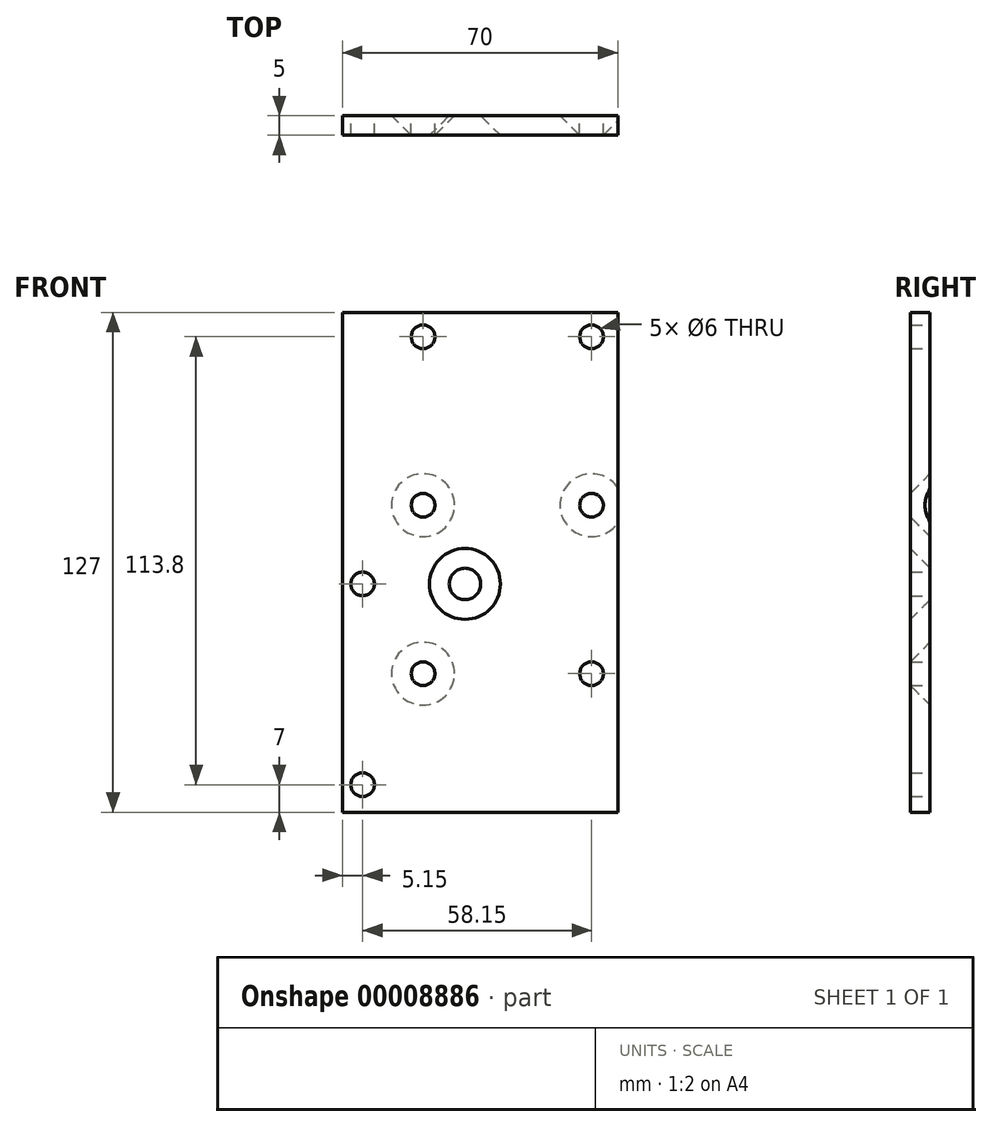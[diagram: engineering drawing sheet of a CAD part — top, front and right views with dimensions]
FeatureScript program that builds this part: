
annotation { "Feature Type Name" : "Feature", "Feature Type Description" : "" }
export const myFeature = defineFeature(function(context is Context, id is Id, definition is map)
    precondition{}
    {
        {
            var Q0;
            Q0=qCreatedBy(makeId("Front.planeOp"),FACE);
            var sketch = newSketch(context, id + "F0", { "sketchPlane" : qUnion([Q0])});
            skLineSegment(sketch, "E0.bottom", {"start": v(-35, 63.5) * mm, "end": v(35, 63.5) * mm});
            skLineSegment(sketch, "E0.top", {"start": v(-35, -63.5) * mm, "end": v(35, -63.5) * mm});
            skLineSegment(sketch, "E0.left", {"start": v(-35, 63.5) * mm, "end": v(-35, -63.5) * mm});
            skLineSegment(sketch, "E0.right", {"start": v(35, 63.5) * mm, "end": v(35, -63.5) * mm});
            skPoint(sketch, "E0.middle", {"position": v(0, 0) * mm});
            skCircle(sketch, "E1", {"center": v(28.3, -28.3) * mm, "radius": 3 * mm});
            skCircle(sketch, "E2.1.0", {"center": v(28.3, 14.5) * mm, "radius": 3 * mm});
            skCircle(sketch, "E2.2.0", {"center": v(-14.5, 14.5) * mm, "radius": 3 * mm});
            skCircle(sketch, "E2.3.0", {"center": v(-14.5, -28.3) * mm, "radius": 3 * mm});
            skPoint(sketch, "E2.center", {"position": v(6.9, -6.9) * mm});
            skCircle(sketch, "E3", {"center": v(-29.85, -56.5) * mm, "radius": 3 * mm});
            skCircle(sketch, "E4", {"center": v(-29.85, -5.5) * mm, "radius": 3 * mm});
            skCircle(sketch, "E5.MirrorC", {"center": v(-14.5, 57.3) * mm, "radius": 3 * mm});
            skCircle(sketch, "E6.MirrorC", {"center": v(28.3, 57.3) * mm, "radius": 3 * mm});
            skLineSegment(sketch, "E7", {"start": v(-47.3, -5.5) * mm, "end": v(40.72, -5.5) * mm, "construction": true});
            skCircle(sketch, "E8", {"center": v(-3.85, -5.5) * mm, "radius": 4 * mm});
            skSolve(sketch);
        }
        {
            var Q0;
            Q0 = qSketchRegion(id + "F0", true);
            extrude(context, id + "F1", {"entities" : qUnion([Q0]), "depth" : 5 * mm});
        }
        {
            var Q0;
            Q0=makeQuery(id+"F1.opExtrude","CAP_EDGE",EDGE,{"disambiguationData":[OSD([sQuery(id+"F0.wireOp",EDGE,"E2.1.0")])],"isStart":true});
            var Q1;
            Q1=makeQuery(id+"F1.opExtrude","CAP_EDGE",EDGE,{"disambiguationData":[OSD([sQuery(id+"F0.wireOp",EDGE,"E2.2.0")])],"isStart":true});
            var Q2;
            Q2=makeQuery(id+"F1.opExtrude","CAP_EDGE",EDGE,{"disambiguationData":[OSD([sQuery(id+"F0.wireOp",EDGE,"E2.3.0")])],"isStart":true});
            chamfer(context, id + "F2", {"entities" : qUnion([Q0, Q1, Q2]), "width" : 5 * mm, "tangentPropagation" : true});
        }
        {
            var Q0;
            Q0=makeQuery(id+"F1.opExtrude","CAP_EDGE",EDGE,{"disambiguationData":[OSD([sQuery(id+"F0.wireOp",EDGE,"E8")])],"isStart":false});
            chamfer(context, id + "F3", {"entities" : qUnion([Q0]), "width" : 5 * mm, "tangentPropagation" : true});
        }
    });
